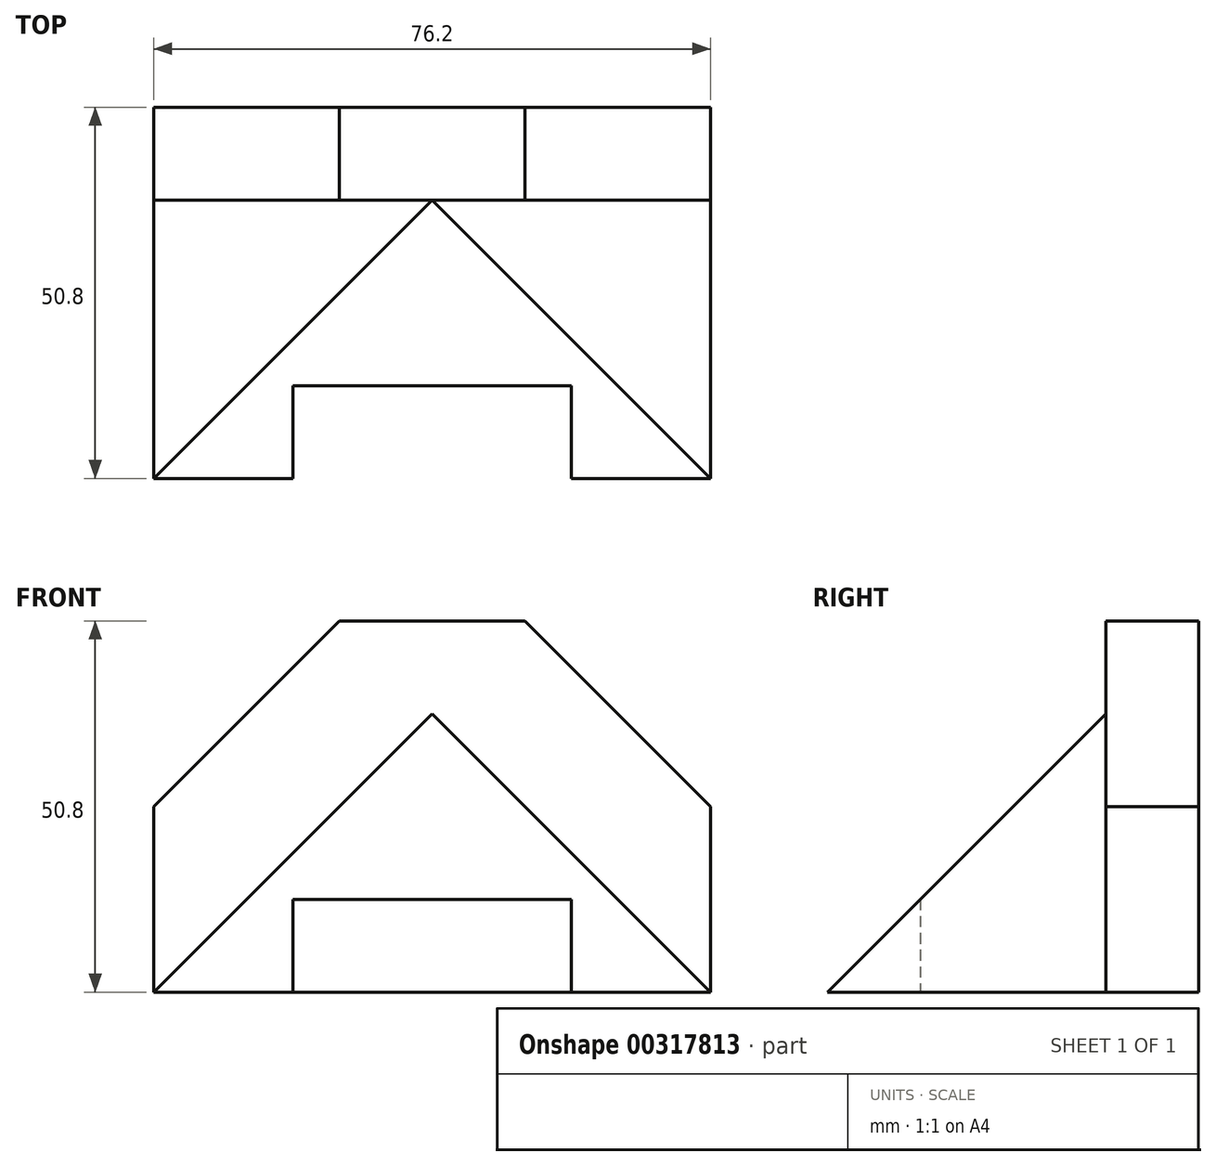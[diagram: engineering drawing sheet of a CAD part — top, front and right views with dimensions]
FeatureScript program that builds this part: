
annotation { "Feature Type Name" : "Feature", "Feature Type Description" : "" }
export const myFeature = defineFeature(function(context is Context, id is Id, definition is map)
    precondition{}
    {
        {
            var Q0;
            Q0=qCreatedBy(makeId("Front.planeOp"),FACE);
            var sketch = newSketch(context, id + "F0", { "sketchPlane" : qUnion([Q0])});
            skLineSegment(sketch, "E0", {"start": v(0, 0) * mm, "end": v(0, 25.4) * mm});
            skLineSegment(sketch, "E1", {"start": v(0, 25.4) * mm, "end": v(25.4, 50.8) * mm});
            skLineSegment(sketch, "E2", {"start": v(25.4, 50.8) * mm, "end": v(50.8, 50.8) * mm});
            skLineSegment(sketch, "E3", {"start": v(50.8, 50.8) * mm, "end": v(76.2, 25.4) * mm});
            skLineSegment(sketch, "E4", {"start": v(76.2, 25.4) * mm, "end": v(76.2, 0) * mm});
            skLineSegment(sketch, "E5", {"start": v(76.2, 0) * mm, "end": v(0, 0) * mm});
            skLineSegment(sketch, "E6", {"start": v(0, 0) * mm, "end": v(38.1, 38.1) * mm});
            skPoint(sketch, "E6.endSnap0", {"position": v(38.1, 50.8) * mm});
            skLineSegment(sketch, "E7", {"start": v(38.1, 38.1) * mm, "end": v(76.2, 0) * mm});
            skLineSegment(sketch, "E8", {"start": v(0, 0) * mm, "end": v(76.2, 0) * mm});
            skSolve(sketch);
        }
        {
            var Q0;
            Q0=makeQuery(id+"F0.imprint","IMPRINT",FACE,{"disambiguationData":[TD([[makeQuery(id+"F0.imprint","IMPRINT",EDGE,{"derivedFrom":sQuery(id+"F0.wireOp",EDGE,"E0")}),-1.0]])]});
            extrude(context, id + "F1", {"entities" : qUnion([Q0]), "depth" : 12.7 * mm});
        }
        {
            var Q0;
            Q0=makeQuery(id+"F0.imprint","IMPRINT",FACE,{"disambiguationData":[TD([[makeQuery(id+"F0.imprint","IMPRINT",EDGE,{"derivedFrom":sQuery(id+"F0.wireOp",EDGE,"E6")}),-1.0]])]});
            extrude(context, id + "F2", {"entities" : qUnion([Q0]), "operationType" : NewBodyOperationType.ADD, "depth" : 50.8 * mm});
        }
        {
            var Q0;
            Q0=makeQuery(id+"F2.opExtrude","CAP_FACE",FACE,{"disambiguationData":[OSD([sQuery(id+"F0.wireOp",EDGE,"E6"),sQuery(id+"F0.wireOp",EDGE,"E7"),sQuery(id+"F0.wireOp",EDGE,"E8")])],"isStart":false});
            var sketch = newSketch(context, id + "F3", { "sketchPlane" : qUnion([Q0])});
            skLineSegment(sketch, "E9", {"start": v(19.05, 19.05) * mm, "end": v(19.05, 0) * mm});
            skLineSegment(sketch, "E10", {"start": v(19.05, 0) * mm, "end": v(57.15, 0) * mm});
            skLineSegment(sketch, "E11", {"start": v(57.15, 19.05) * mm, "end": v(57.15, 0) * mm});
            skLineSegment(sketch, "E12", {"start": v(19.05, 19.05) * mm, "end": v(38.1, 38.1) * mm});
            skLineSegment(sketch, "E13", {"start": v(38.1, 38.1) * mm, "end": v(57.15, 19.05) * mm});
            skSolve(sketch);
        }
        {
            var Q0;
            Q0 = qSketchRegion(id + "F3", true);
            extrude(context, id + "F4", {"entities" : qUnion([Q0]), "operationType" : NewBodyOperationType.REMOVE, "oppositeDirection" : true, "depth" : 12.7 * mm});
        }
        {
            var Q0;
            Q0=qCreatedBy(makeId("Right.planeOp"),FACE);
            var sketch = newSketch(context, id + "F5", { "sketchPlane" : qUnion([Q0])});
            skLineSegment(sketch, "E14", {"start": v(-50.8, 0) * mm, "end": v(-12.7, 38.1) * mm});
            skLineSegment(sketch, "E15", {"start": v(-12.7, 38.1) * mm, "end": v(-50.8, 38.1) * mm});
            skLineSegment(sketch, "E16", {"start": v(-50.8, 38.1) * mm, "end": v(-50.8, 0) * mm});
            skSolve(sketch);
        }
        {
            var Q0;
            Q0 = qSketchRegion(id + "F5", true);
            extrude(context, id + "F6", {"entities" : qUnion([Q0]), "operationType" : NewBodyOperationType.REMOVE, "endBound" : BoundingType.THROUGH_ALL, "depth" : 25.4 * mm});
        }
    });
